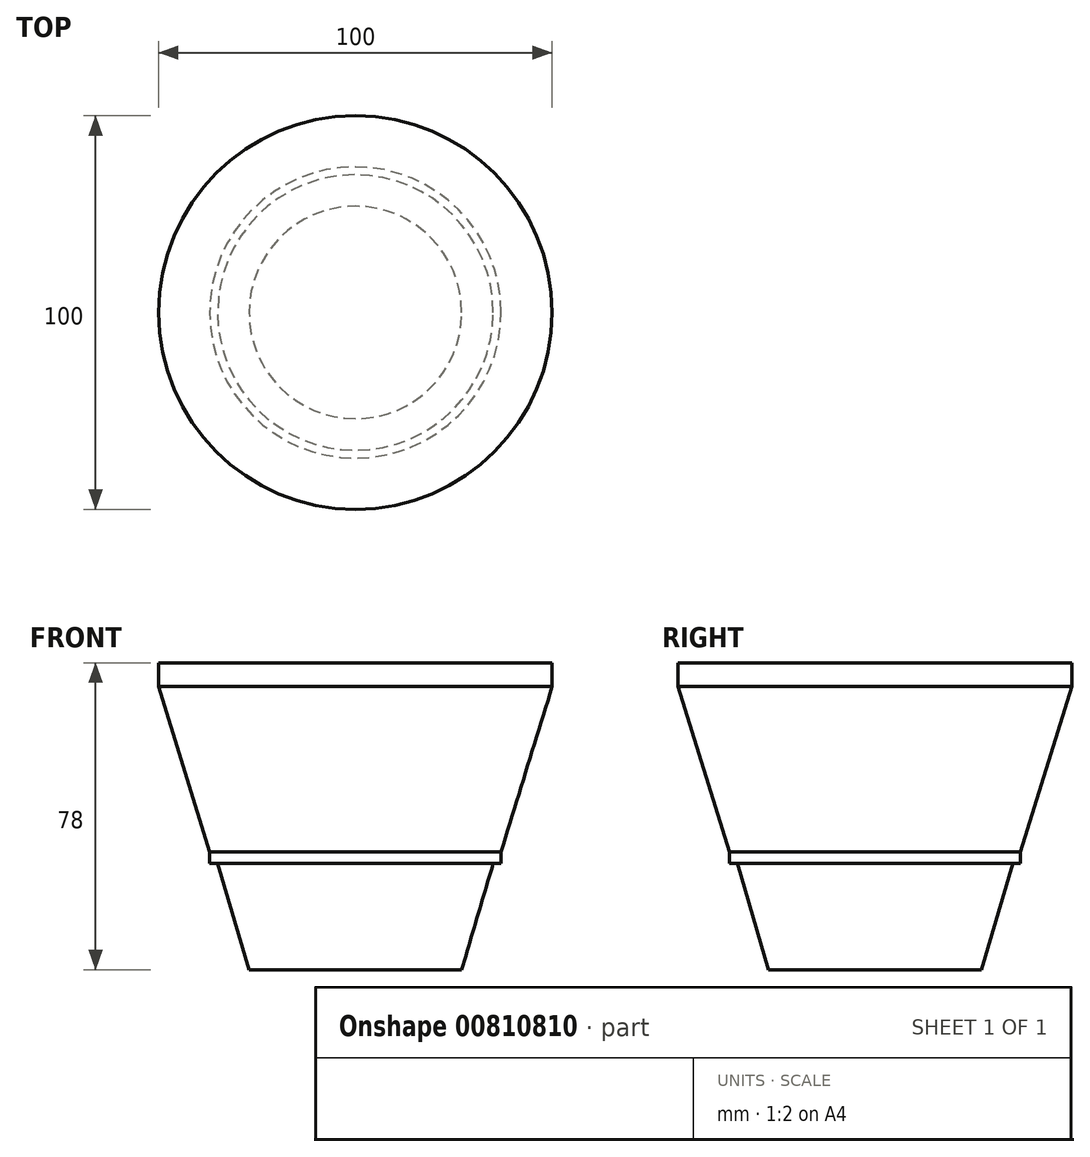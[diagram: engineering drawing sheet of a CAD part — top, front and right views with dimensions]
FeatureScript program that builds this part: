
annotation { "Feature Type Name" : "Feature", "Feature Type Description" : "" }
export const myFeature = defineFeature(function(context is Context, id is Id, definition is map)
    precondition{}
    {
        {
            var Q0;
            Q0=qCreatedBy(makeId("Front.planeOp"),FACE);
            var sketch = newSketch(context, id + "F0", { "sketchPlane" : qUnion([Q0])});
            skLineSegment(sketch, "E0", {"start": v(0, 0) * mm, "end": v(27, 0) * mm});
            skLineSegment(sketch, "E1", {"start": v(27, 0) * mm, "end": v(35, 27) * mm});
            skLineSegment(sketch, "E2", {"start": v(35, 27) * mm, "end": v(3, 27) * mm});
            skLineSegment(sketch, "E3", {"start": v(3, 27) * mm, "end": v(3, 21) * mm});
            skLineSegment(sketch, "E4", {"start": v(3, 21) * mm, "end": v(0, 21) * mm});
            skLineSegment(sketch, "E5", {"start": v(0, 21) * mm, "end": v(0, 0) * mm});
            skLineSegment(sketch, "E6", {"start": v(37, 30) * mm, "end": v(50, 72) * mm});
            skLineSegment(sketch, "E7", {"start": v(50, 72) * mm, "end": v(43.12, 72) * mm});
            skLineSegment(sketch, "E8", {"start": v(43.12, 72) * mm, "end": v(43.12, 66) * mm});
            skLineSegment(sketch, "E9", {"start": v(43.12, 66) * mm, "end": v(35.87, 66) * mm});
            skLineSegment(sketch, "E10", {"start": v(10.5, 42) * mm, "end": v(10.5, 36) * mm});
            skLineSegment(sketch, "E11", {"start": v(10.5, 36) * mm, "end": v(4, 36) * mm});
            skLineSegment(sketch, "E12", {"start": v(4, 36) * mm, "end": v(4, 30) * mm});
            skLineSegment(sketch, "E13", {"start": v(17.87, 30) * mm, "end": v(17.87, 36) * mm});
            skLineSegment(sketch, "E14", {"start": v(17.87, 36) * mm, "end": v(25.12, 36) * mm});
            skLineSegment(sketch, "E15", {"start": v(25.12, 36) * mm, "end": v(25.12, 30) * mm});
            skLineSegment(sketch, "E16", {"start": v(25.12, 30) * mm, "end": v(37, 30) * mm});
            skLineSegment(sketch, "E17", {"start": v(17.87, 30) * mm, "end": v(4, 30) * mm});
            skLineSegment(sketch, "E18", {"start": v(0, 21) * mm, "end": v(0, 15) * mm});
            skLineSegment(sketch, "E19", {"start": v(0, 15) * mm, "end": v(23, 15) * mm});
            skLineSegment(sketch, "E20", {"start": v(23, 15) * mm, "end": v(23, 18) * mm});
            skLineSegment(sketch, "E21", {"start": v(23, 18) * mm, "end": v(20, 18) * mm});
            skLineSegment(sketch, "E22", {"start": v(20, 18) * mm, "end": v(20, 21) * mm});
            skLineSegment(sketch, "E23", {"start": v(20, 21) * mm, "end": v(23, 21) * mm});
            skLineSegment(sketch, "E24", {"start": v(23, 21) * mm, "end": v(23, 24) * mm});
            skLineSegment(sketch, "E25", {"start": v(23, 24) * mm, "end": v(20, 24) * mm});
            skLineSegment(sketch, "E26", {"start": v(20, 24) * mm, "end": v(20, 27) * mm});
            skLineSegment(sketch, "E27", {"start": v(37, 30) * mm, "end": v(37, 27) * mm});
            skLineSegment(sketch, "E28", {"start": v(37, 27) * mm, "end": v(35, 27) * mm});
            skLineSegment(sketch, "E29", {"start": v(3, 27) * mm, "end": v(3, 30) * mm});
            skLineSegment(sketch, "E30", {"start": v(3, 30) * mm, "end": v(4, 30) * mm});
            skLineSegment(sketch, "E31", {"start": v(35.87, 66) * mm, "end": v(35.87, 72) * mm});
            skLineSegment(sketch, "E32", {"start": v(35.87, 72) * mm, "end": v(39, 78) * mm});
            skLineSegment(sketch, "E33", {"start": v(39, 78) * mm, "end": v(32.87, 78) * mm});
            skLineSegment(sketch, "E34", {"start": v(32.87, 78) * mm, "end": v(32.87, 42) * mm});
            skLineSegment(sketch, "E35", {"start": v(35.87, 51) * mm, "end": v(38.87, 51) * mm});
            skLineSegment(sketch, "E36", {"start": v(38.87, 51) * mm, "end": v(38.87, 54) * mm});
            skLineSegment(sketch, "E37", {"start": v(38.87, 54) * mm, "end": v(35.88, 54) * mm});
            skLineSegment(sketch, "E38", {"start": v(35.88, 54) * mm, "end": v(35.88, 57) * mm});
            skLineSegment(sketch, "E39", {"start": v(35.87, 57) * mm, "end": v(38.87, 57) * mm});
            skLineSegment(sketch, "E40", {"start": v(38.87, 57) * mm, "end": v(38.87, 60) * mm});
            skLineSegment(sketch, "E41", {"start": v(38.87, 60) * mm, "end": v(35.87, 60) * mm});
            skLineSegment(sketch, "E42", {"start": v(35.87, 60) * mm, "end": v(35.87, 66) * mm});
            skLineSegment(sketch, "E43", {"start": v(35.87, 51) * mm, "end": v(35.87, 39) * mm});
            skLineSegment(sketch, "E44", {"start": v(32.87, 42) * mm, "end": v(10.5, 42) * mm});
            skLineSegment(sketch, "E45", {"start": v(32.87, 78) * mm, "end": v(0, 78) * mm});
            skLineSegment(sketch, "E46", {"start": v(0, 78) * mm, "end": v(0, 21) * mm});
            skLineSegment(sketch, "E47", {"start": v(50, 72) * mm, "end": v(50, 78) * mm});
            skLineSegment(sketch, "E48", {"start": v(50, 78) * mm, "end": v(39, 78) * mm});
            skLineSegment(sketch, "E49", {"start": v(35.87, 39) * mm, "end": v(25.12, 39) * mm});
            skLineSegment(sketch, "E50", {"start": v(25.12, 39) * mm, "end": v(25.12, 36) * mm});
            skSolve(sketch);
        }
        {
            var Q0;
            Q0 = qSketchRegion(id + "F0", true);
            var Q1;
            Q1=sQuery(id+"F0.wireOp",EDGE,"E46");
            revolve(context, id + "F1", {"surfaceOperationType" : NewSurfaceOperationType.NEW, "entities" : qUnion([Q0]), "axis" : qUnion([Q1]), "revolveType" : RevolveType.FULL});
        }
    });
